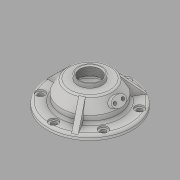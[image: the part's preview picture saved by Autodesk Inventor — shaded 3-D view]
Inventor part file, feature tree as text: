
AUTODESK INVENTOR PART (.ipt)
format: ipt  version: 2020 (Build 240168000, 168)  size: 346,112 bytes
history: native  units: mm
features: sketch x9, hole x4, thread x3, extrude x2, pattern_circular x2, plane x2, revolve x1
ambient origin geometry x8: Origin, YZ Plane, XZ Plane, XY Plane, X Axis, Y Axis, Z Axis, Center Point
bodies: Solid1 (feature_tree)
feature tree (23):
  revolve  "Revolution1"  [1 undecoded]
  extrude  "Extrusion1"  Depth=6.0mm
  hole  "Hole1"  [1 undecoded]
  hole  "Hole2"  [1 undecoded]
  pattern_circular  "Circular Pattern1"  Count=4  [1 undecoded]
  pattern_circular  "Circular Pattern2"  Angle=90.0deg  [1 undecoded]
  plane  "Work Plane1"
  sketch  "Sketch5"  dims[d9=11.0mm d10=40.0mm]
  sketch  "Sketch6"  dims[d11=30.0deg]
  plane  "Work Plane2"
  extrude  "Extrusion2"  Depth=2.0mm
  hole  "Hole3"  [1 undecoded]
  hole  "Hole4"  [1 undecoded]
  thread  "Thread1"  [1 undecoded]
  thread  "Thread2"  [1 undecoded]
  thread  "Thread3"  [1 undecoded]
  sketch  "Sketch1"  dims[d0=104.0mm d2=54.0mm]
  sketch  "Sketch2"  dims[d3=30.0mm d4=6.0mm]
  sketch  "Sketch3"  dims[d5=15.0mm d6=70.0mm]
  sketch  "Sketch4"  dims[d7=50.0mm d8=18.0mm]
  sketch  "Sketch7"  dims[d12=24.0mm]
  sketch  "Sketch8"  dims[d13=3.0mm]
  sketch  "Sketch9"  dims[d14=3.0mm d15=90.0deg d16=3.0mm d17=3.0mm d18=6.0mm d19=0.0mm d20=90.0mm d21=6.5mm d22=6.0mm d23=11.0mm d24=2.0mm d25=90.0deg d26=8.0mm d27=20.594885mm d28=90.0mm d29=4.0mm d30=6.0mm d31=11.0mm d32=2.0mm d33=90.0deg d34=8.0mm d35=20.594885mm d36=30.0mm d37=360.0deg d39=-1.5mm d40=5.0mm d41=0.0mm d43=12.0mm d44=18.0mm d45=10.0mm d46=4.0mm d47=6.0mm d48=4.0mm d49=2.0mm d50=90.0deg d51=8.0mm d52=20.594885mm d53=30.0mm d54=35.0mm d55=25.4mm d56=6.0mm d57=28.0mm d58=2.0mm d59=90.0deg d60=8.0mm d61=20.594885mm d62=60.0mm d63=360.0deg d65=9.7mm d66=0.0mm d67=5.0mm d68=0.0mm d69=5.0mm d70=0.0mm]
note: 10 required parameter values undecoded (feature->parameter linkage not recoverable at this tier; creation-order binding heuristic only, values carry confidence <= 0.55)